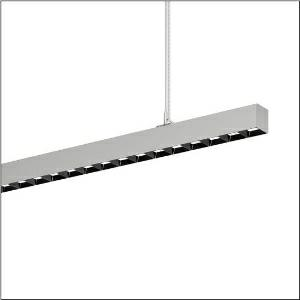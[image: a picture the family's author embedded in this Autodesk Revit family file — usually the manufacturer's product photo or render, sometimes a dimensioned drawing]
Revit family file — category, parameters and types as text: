
# Revit family: silica_r__21_51mx31tat7s_2b6e
name_source: partatom
category: Lighting Fixtures
units: mm (PartAtom-declared; Revit-internal decimal feet)

## family parameters
Cut with Voids When Loaded = No
Host = Face
Light Source = No
Part Type = Normal
Room Calculation Point = No
Round Connector Dimension = Use Diameter
Shared = No

## types (1)
- --- (1 x LED, 6220 lm, 53.5 W, 6500K)
    Apparent Load = 54 VA
    CIE Flux Codes = 85 99 100 60 100
    Color Rendering = 80
    Color Temperature = 6500K
    Default Elevation = 1800 mm
    Description = Silica® 21, office luminaire, primary light control with darklight reflector, of PMMA, black, CAT 2 (L<= 3000cd/m²), light emission: direct/indirect distribution, primary light characteristic: symmetric, installation type: suspended mounting, LED, rated luminous flux: 6.220lm, luminous efficacy: 111lm/W, light colour: 8tw, colour temperature: 2700..6500K, control gear: ECG DALI, with terminal, 3+2-pole, max. 2.5mm², mains connection: 220..240V, AC, 50/60Hz, rated input power: 56.2W, luminaire housing, of aluminium, metallic grey (RAL 9006), length: 1.204mm, width: 53mm, height: 53mm, protection rating (complete): IP20, insulation class (complete): insulation class I (protective earthing), certification: CE, permissible operating ambient temperature: 0..+35°C, standard: EN 50419, packaging unit: 1 piece
    Height = 53 mm
    Lamp = 1 x LED
    Lamp Light Flux = 6220 lm
    Lamp Power = 53.5 W
    Lamp count = 1
    Length = 1204 mm
    Luminous efficacy = 116 lm/W
    Manufacturer = Siteco
    ModVariant = No
    Model = 51MX31TAT7S
    Mounting Place = Ceiling
    Mounting Type = Pendant
    Number of Poles = 1
    OnlyDefault = Yes
    Power Factor = 1
    Product Name = Silica® 21
    Product group = office luminaire | ceiling pendant
    ProductGroupID = 905
    Protection Class = Protection class I
    Protection Degree = IP 20
    RLX_Detail_Level = 1
    RlxData = <blob elided: 41281 chars, md5=6ba80575>
    Socket = socket
    Standby Power = 0 W
    System Light Flux = 6220 lm
    System Power = 54 W
    Type Comments = individual setting
    Type Image = l_1251731.jpg
    URL = http://relux.com
    VarID = @adj_045963
    Voltage = 0 V
    Weight = 0.00 kg
    Width = 53 mm

## geometry (parser evidence)
native form markers: Blend x4, Sweep x13
no freeform markers — native parametric forms only
